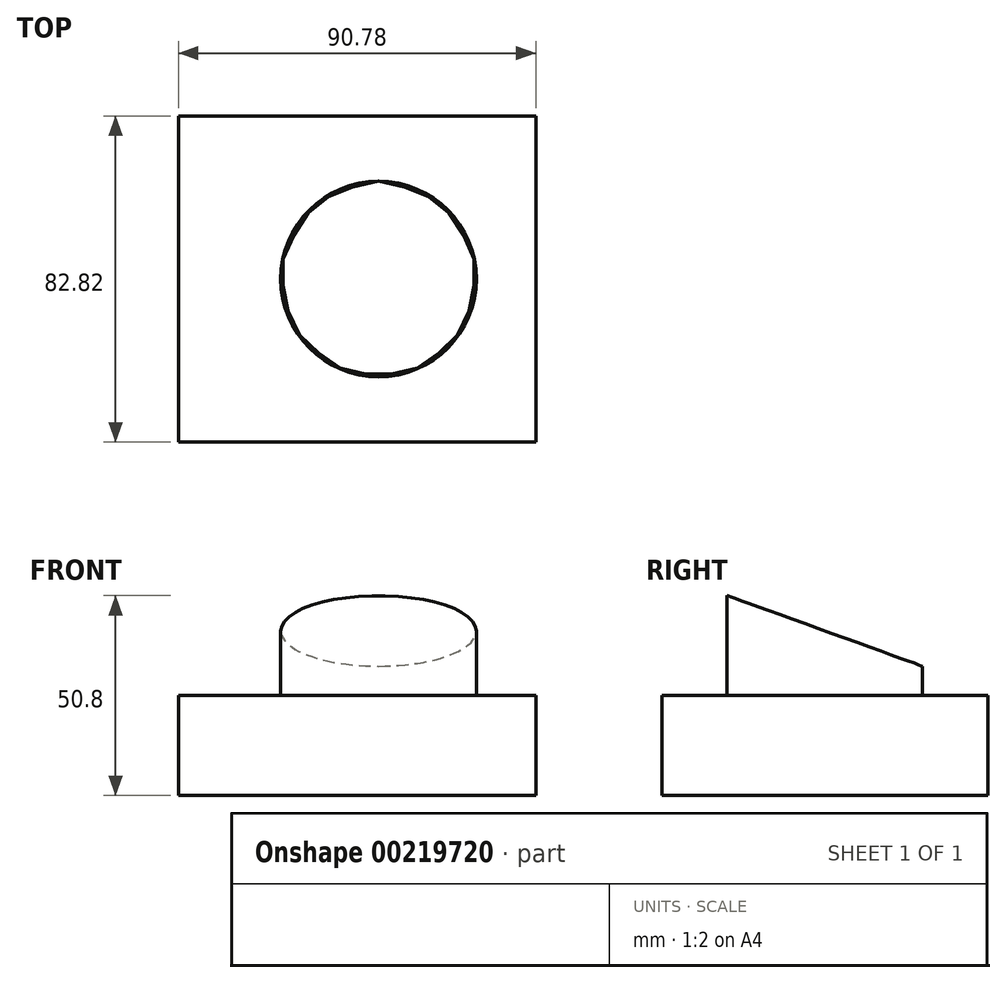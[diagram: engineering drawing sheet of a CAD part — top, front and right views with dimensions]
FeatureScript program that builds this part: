
annotation { "Feature Type Name" : "Feature", "Feature Type Description" : "" }
export const myFeature = defineFeature(function(context is Context, id is Id, definition is map)
    precondition{}
    {
        {
            var Q0;
            Q0=qCreatedBy(makeId("Top.planeOp"),FACE);
            var sketch = newSketch(context, id + "F0", { "sketchPlane" : qUnion([Q0])});
            skLineSegment(sketch, "E0.bottom", {"start": v(-45.39, 41.41) * mm, "end": v(45.39, 41.41) * mm});
            skLineSegment(sketch, "E0.top", {"start": v(-45.39, -41.41) * mm, "end": v(45.39, -41.41) * mm});
            skLineSegment(sketch, "E0.left", {"start": v(-45.39, 41.41) * mm, "end": v(-45.39, -41.41) * mm});
            skLineSegment(sketch, "E0.right", {"start": v(45.39, 41.41) * mm, "end": v(45.39, -41.41) * mm});
            skPoint(sketch, "E0.middle", {"position": v(0, 0) * mm});
            skSolve(sketch);
        }
        {
            var Q0;
            Q0=makeQuery(id+"F0.imprint","IMPRINT",FACE,{"disambiguationData":[TD([[makeQuery(id+"F0.imprint","IMPRINT",EDGE,{"derivedFrom":sQuery(id+"F0.wireOp",EDGE,"E0.bottom")}),-1.0]])]});
            extrude(context, id + "F1", {"entities" : qUnion([Q0]), "depth" : 25.4 * mm});
        }
        {
            var Q0;
            Q0=makeQuery(id+"F1.opExtrude","CAP_FACE",FACE,{"disambiguationData":[OSD([sQuery(id+"F0.wireOp",EDGE,"E0.bottom"),sQuery(id+"F0.wireOp",EDGE,"E0.top"),sQuery(id+"F0.wireOp",EDGE,"E0.left"),sQuery(id+"F0.wireOp",EDGE,"E0.right")])],"isStart":false});
            var sketch = newSketch(context, id + "F2", { "sketchPlane" : qUnion([Q0])});
            skCircle(sketch, "E1", {"center": v(5.45, 0) * mm, "radius": 24.86 * mm});
            skSolve(sketch);
        }
        {
            var Q0;
            Q0=makeQuery(id+"F2.imprint","IMPRINT",FACE,{"disambiguationData":[TD([[makeQuery(id+"F2.imprint","IMPRINT",EDGE,{"derivedFrom":sQuery(id+"F2.wireOp",EDGE,"E1")}),1.0]])]});
            extrude(context, id + "F3", {"entities" : qUnion([Q0]), "operationType" : NewBodyOperationType.ADD, "depth" : 25.4 * mm});
        }
        {
            var Q0;
            Q0=makeQuery(id+"F1.opExtrude","SWEPT_FACE",FACE,{"disambiguationData":[OSD([sQuery(id+"F0.wireOp",EDGE,"E0.right")])]});
            var sketch = newSketch(context, id + "F4", { "sketchPlane" : qUnion([Q0])});
            skLineSegment(sketch, "E2.0", {"start": v(-24.86, 50.8) * mm, "end": v(24.86, 50.8) * mm});
            skLineSegment(sketch, "E3", {"start": v(24.86, 50.8) * mm, "end": v(24.86, 32.84) * mm});
            skLineSegment(sketch, "E4", {"start": v(-24.86, 50.8) * mm, "end": v(24.86, 32.84) * mm});
            skSolve(sketch);
        }
        {
            var Q0;
            Q0 = qSketchRegion(id + "F4", true);
            extrude(context, id + "F5", {"entities" : qUnion([Q0]), "operationType" : NewBodyOperationType.REMOVE, "endBound" : BoundingType.THROUGH_ALL, "oppositeDirection" : true, "depth" : 25.4 * mm});
        }
    });
